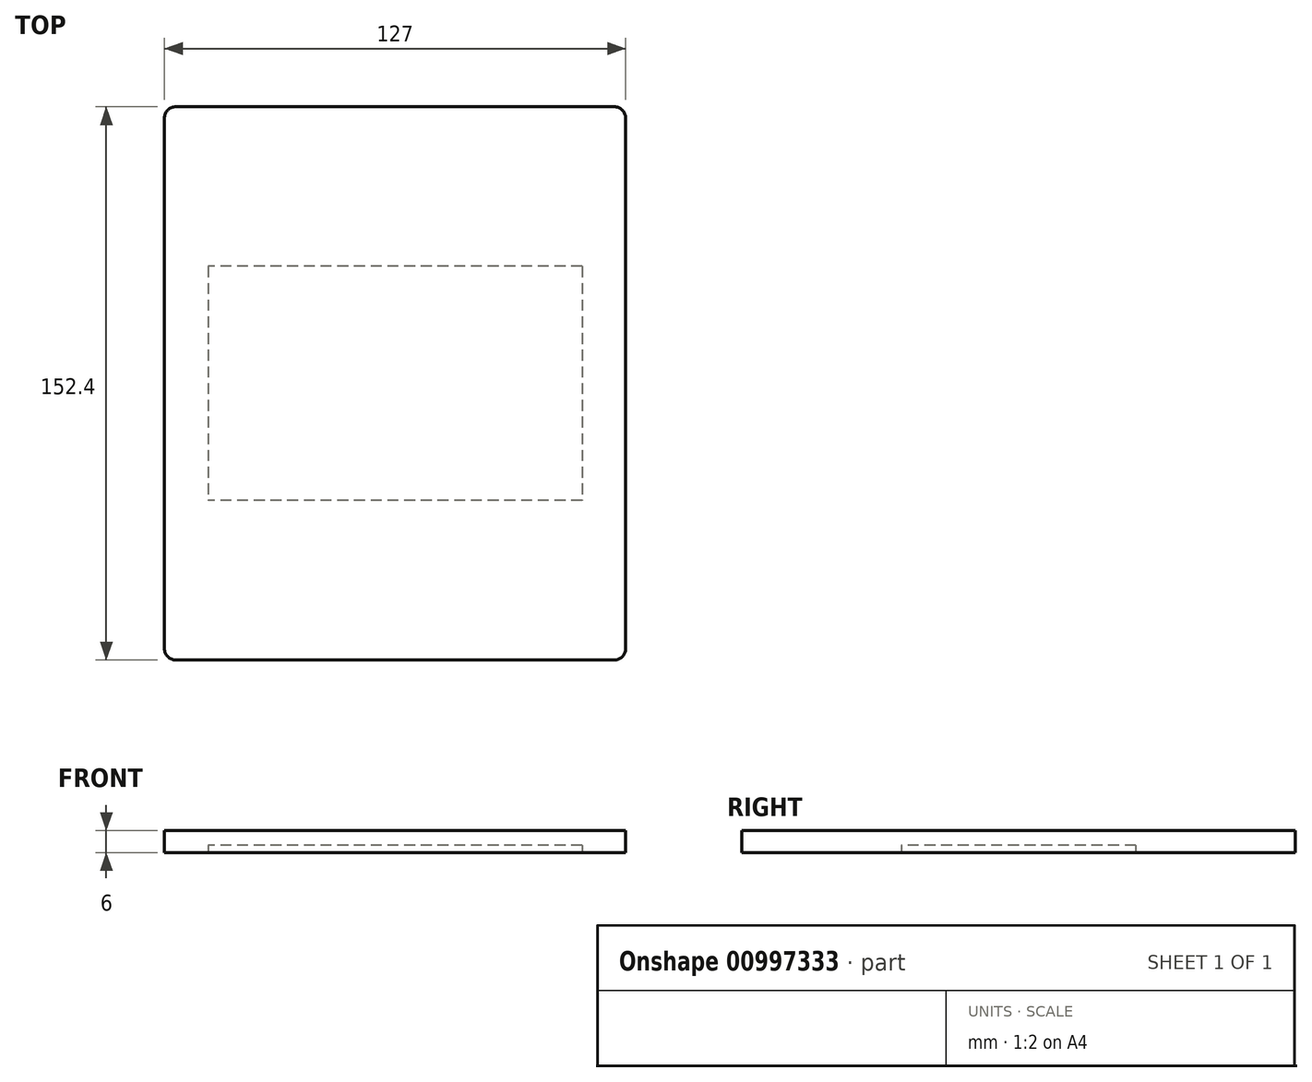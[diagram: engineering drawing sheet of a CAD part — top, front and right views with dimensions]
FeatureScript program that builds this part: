
annotation { "Feature Type Name" : "Feature", "Feature Type Description" : "" }
export const myFeature = defineFeature(function(context is Context, id is Id, definition is map)
    precondition{}
    {
        {
            var Q0;
            Q0=qCreatedBy(makeId("Top.planeOp"),FACE);
            var sketch = newSketch(context, id + "F0", { "sketchPlane" : qUnion([Q0])});
            skLineSegment(sketch, "E0.bottom", {"start": v(51.5, 32.25) * mm, "end": v(-51.5, 32.25) * mm});
            skLineSegment(sketch, "E0.top", {"start": v(51.5, -32.25) * mm, "end": v(-51.5, -32.25) * mm});
            skLineSegment(sketch, "E0.left", {"start": v(51.5, 32.25) * mm, "end": v(51.5, -32.25) * mm});
            skLineSegment(sketch, "E0.right", {"start": v(-51.5, 32.25) * mm, "end": v(-51.5, -32.25) * mm});
            skPoint(sketch, "E0.middle", {"position": v(0, 0) * mm});
            skLineSegment(sketch, "E1.bottom", {"start": v(63.5, 76.2) * mm, "end": v(-63.5, 76.2) * mm});
            skLineSegment(sketch, "E1.top", {"start": v(63.5, -76.2) * mm, "end": v(-63.5, -76.2) * mm});
            skLineSegment(sketch, "E1.left", {"start": v(63.5, 76.2) * mm, "end": v(63.5, -76.2) * mm});
            skLineSegment(sketch, "E1.right", {"start": v(-63.5, 76.2) * mm, "end": v(-63.5, -76.2) * mm});
            skSolve(sketch);
        }
        {
            var Q0;
            Q0=makeQuery(id+"F0.imprint","IMPRINT",FACE,{"disambiguationData":[TD([[makeQuery(id+"F0.imprint","IMPRINT",EDGE,{"derivedFrom":sQuery(id+"F0.wireOp",EDGE,"E0.bottom")}),-1.0]])]});
            var Q1;
            Q1=makeQuery(id+"F0.imprint","IMPRINT",FACE,{"disambiguationData":[TD([[makeQuery(id+"F0.imprint","IMPRINT",EDGE,{"derivedFrom":sQuery(id+"F0.wireOp",EDGE,"E0.bottom")}),1.0]])]});
            extrude(context, id + "F1", {"entities" : qUnion([Q0, Q1]), "depth" : 6 * mm, "offsetDistance" : 25.4 * mm});
        }
        {
            var Q0;
            Q0=makeQuery(id+"F0.imprint","IMPRINT",FACE,{"disambiguationData":[TD([[makeQuery(id+"F0.imprint","IMPRINT",EDGE,{"derivedFrom":sQuery(id+"F0.wireOp",EDGE,"E0.bottom")}),1.0]])]});
            extrude(context, id + "F2", {"entities" : qUnion([Q0]), "operationType" : NewBodyOperationType.REMOVE, "depth" : 2 * mm, "offsetDistance" : 25.4 * mm});
        }
        {
            var Q0;
            Q0=makeQuery(id+"F1.opExtrude","SWEPT_EDGE",EDGE,{"disambiguationData":[OSD([sQuery(id+"F0.wireOp",EDGE,"E1.top"),sQuery(id+"F0.wireOp",EDGE,"E1.left")])]});
            var Q1;
            Q1=makeQuery(id+"F1.opExtrude","SWEPT_EDGE",EDGE,{"disambiguationData":[OSD([sQuery(id+"F0.wireOp",EDGE,"E1.top"),sQuery(id+"F0.wireOp",EDGE,"E1.right")])]});
            var Q2;
            Q2=makeQuery(id+"F1.opExtrude","SWEPT_EDGE",EDGE,{"disambiguationData":[OSD([sQuery(id+"F0.wireOp",EDGE,"E1.bottom"),sQuery(id+"F0.wireOp",EDGE,"E1.left")])]});
            var Q3;
            Q3=makeQuery(id+"F1.opExtrude","SWEPT_EDGE",EDGE,{"disambiguationData":[OSD([sQuery(id+"F0.wireOp",EDGE,"E1.bottom"),sQuery(id+"F0.wireOp",EDGE,"E1.right")])]});
            fillet(context, id + "F3", {"entities" : qUnion([Q0, Q1, Q2, Q3]), "radius" : 3.17 * mm, "tangentPropagation" : true, "allowEdgeOverflow" : false});
        }
    });
